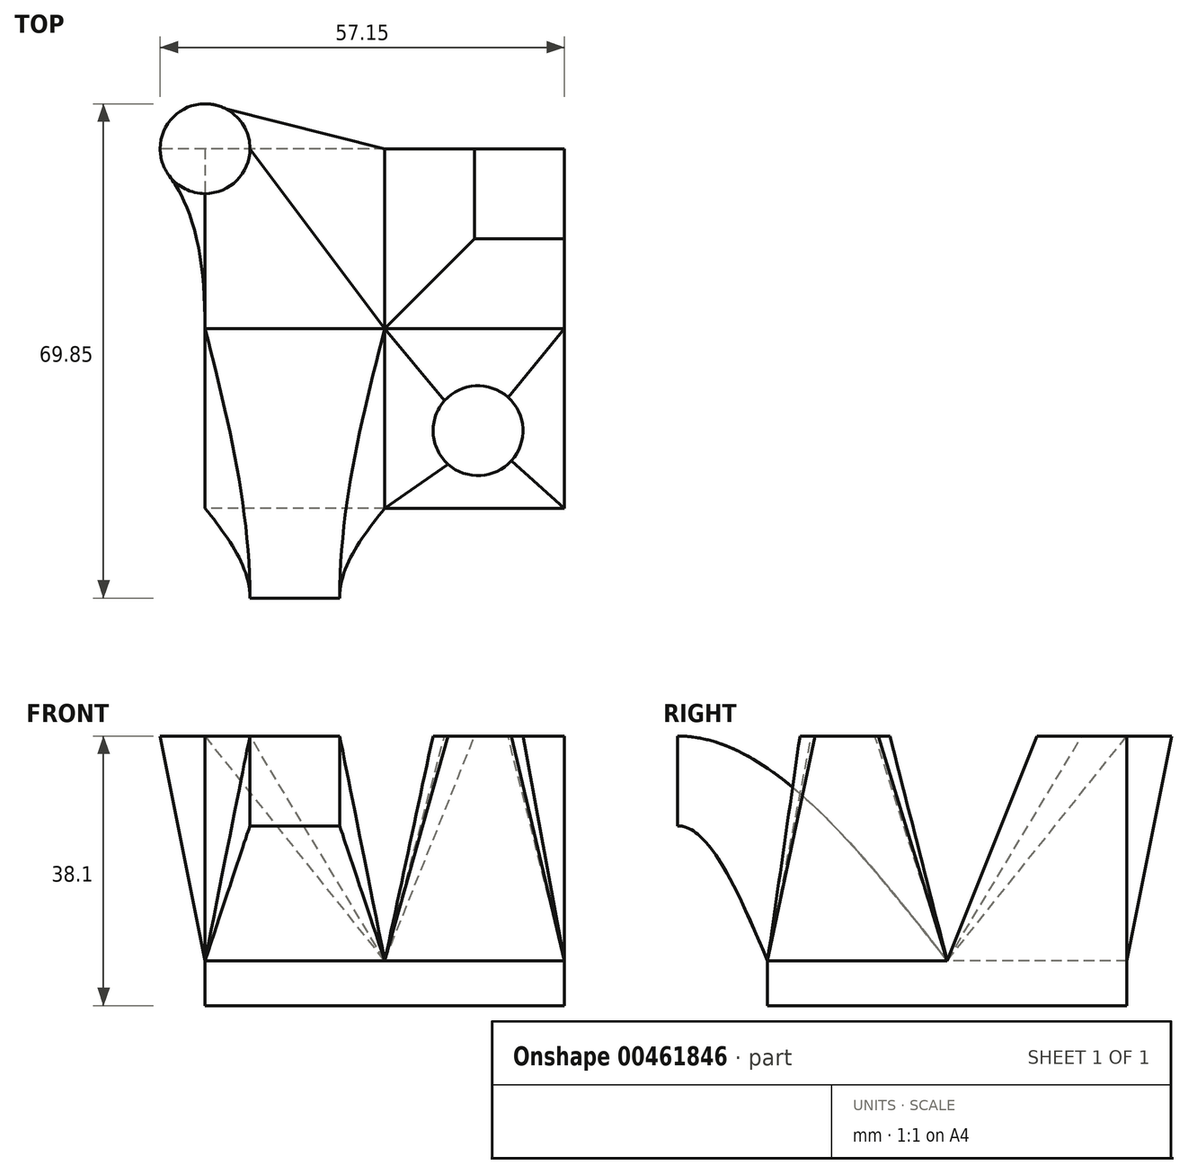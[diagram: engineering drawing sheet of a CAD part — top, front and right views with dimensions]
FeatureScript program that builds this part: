
annotation { "Feature Type Name" : "Feature", "Feature Type Description" : "" }
export const myFeature = defineFeature(function(context is Context, id is Id, definition is map)
    precondition{}
    {
        {
            var Q0;
            Q0=qCreatedBy(makeId("Top.planeOp"),FACE);
            var sketch = newSketch(context, id + "F0", { "sketchPlane" : qUnion([Q0])});
            skLineSegment(sketch, "E0.bottom", {"start": v(25.4, 25.4) * mm, "end": v(-25.4, 25.4) * mm});
            skLineSegment(sketch, "E0.top", {"start": v(25.4, -25.4) * mm, "end": v(-25.4, -25.4) * mm});
            skLineSegment(sketch, "E0.left", {"start": v(25.4, 25.4) * mm, "end": v(25.4, -25.4) * mm});
            skLineSegment(sketch, "E0.right", {"start": v(-25.4, 25.4) * mm, "end": v(-25.4, -25.4) * mm});
            skPoint(sketch, "E0.middle", {"position": v(0, 0) * mm});
            skSolve(sketch);
        }
        {
            var Q0;
            Q0=makeQuery(id+"F0.imprint","IMPRINT",FACE,{"disambiguationData":[TD([[makeQuery(id+"F0.imprint","IMPRINT",EDGE,{"derivedFrom":sQuery(id+"F0.wireOp",EDGE,"E0.bottom")}),1.0]])]});
            extrude(context, id + "F1", {"entities" : qUnion([Q0]), "depth" : 6.35 * mm});
        }
        {
            var Q0;
            Q0=makeQuery(id+"F1.opExtrude","CAP_FACE",FACE,{"disambiguationData":[OSD([sQuery(id+"F0.wireOp",EDGE,"E0.bottom"),sQuery(id+"F0.wireOp",EDGE,"E0.top"),sQuery(id+"F0.wireOp",EDGE,"E0.left"),sQuery(id+"F0.wireOp",EDGE,"E0.right")])],"isStart":false});
            var sketch = newSketch(context, id + "F2", { "sketchPlane" : qUnion([Q0])});
            skLineSegment(sketch, "E1.bottom", {"start": v(0, 0) * mm, "end": v(25.4, 0) * mm});
            skLineSegment(sketch, "E1.top", {"start": v(0, 25.4) * mm, "end": v(25.4, 25.4) * mm});
            skLineSegment(sketch, "E1.left", {"start": v(0, 0) * mm, "end": v(0, 25.4) * mm});
            skLineSegment(sketch, "E1.right", {"start": v(25.4, 0) * mm, "end": v(25.4, 25.4) * mm});
            skSolve(sketch);
        }
        {
            var Q0;
            Q0=qCreatedBy(makeId("Top.planeOp"),FACE);
            cPlane(context, id + "F3", {"entities" : qUnion([Q0]), "cplaneType" : CPlaneType.OFFSET, "offset" : 38.1 * mm, "width" : 152.4 * mm, "height" : 152.4 * mm});
        }
        {
            var Q0;
            Q0=qCreatedBy(id+"F3.planeOp",FACE);
            var sketch = newSketch(context, id + "F4", { "sketchPlane" : qUnion([Q0])});
            skLineSegment(sketch, "E2.bottom", {"start": v(25.4, 25.4) * mm, "end": v(12.7, 25.4) * mm});
            skLineSegment(sketch, "E2.top", {"start": v(25.4, 12.7) * mm, "end": v(12.7, 12.7) * mm});
            skLineSegment(sketch, "E2.left", {"start": v(25.4, 25.4) * mm, "end": v(25.4, 12.7) * mm});
            skLineSegment(sketch, "E2.right", {"start": v(12.7, 25.4) * mm, "end": v(12.7, 12.7) * mm});
            skSolve(sketch);
        }
        {
            var Q1;
            Q1=makeQuery(id+"F2.imprint","IMPRINT",FACE,{"disambiguationData":[TD([[makeQuery(id+"F2.imprint","IMPRINT",EDGE,{"derivedFrom":sQuery(id+"F2.wireOp",EDGE,"E1.bottom")}),1.0]])]});
            var Q2;
            Q2=makeQuery(id+"F4.imprint","IMPRINT",FACE,{"disambiguationData":[TD([[makeQuery(id+"F4.imprint","IMPRINT",EDGE,{"derivedFrom":sQuery(id+"F4.wireOp",EDGE,"E2.bottom")}),1.0]])]});
            loft(context, id + "F5", {"operationType" : NewBodyOperationType.ADD, "sheetProfilesArray" : [{ "sheetProfileEntities" : qUnion([Q1]) }, { "sheetProfileEntities" : qUnion([Q2]) }]});
        }
        {
            var Q0;
            Q0=makeQuery(id+"F1.opExtrude","CAP_FACE",FACE,{"disambiguationData":[OSD([sQuery(id+"F0.wireOp",EDGE,"E0.bottom"),sQuery(id+"F0.wireOp",EDGE,"E0.top"),sQuery(id+"F0.wireOp",EDGE,"E0.left"),sQuery(id+"F0.wireOp",EDGE,"E0.right")])],"isStart":false});
            var sketch = newSketch(context, id + "F6", { "sketchPlane" : qUnion([Q0])});
            skLineSegment(sketch, "E3.bottom", {"start": v(0, 0) * mm, "end": v(25.4, 0) * mm});
            skLineSegment(sketch, "E3.top", {"start": v(0, -25.4) * mm, "end": v(25.4, -25.4) * mm});
            skLineSegment(sketch, "E3.left", {"start": v(0, 0) * mm, "end": v(0, -25.4) * mm});
            skLineSegment(sketch, "E3.right", {"start": v(25.4, 0) * mm, "end": v(25.4, -25.4) * mm});
            skSolve(sketch);
        }
        {
            var Q0;
            Q0=qCreatedBy(id+"F3.planeOp",FACE);
            var sketch = newSketch(context, id + "F7", { "sketchPlane" : qUnion([Q0])});
            skCircle(sketch, "E4", {"center": v(13.18, -14.46) * mm, "radius": 6.35 * mm});
            skLineSegment(sketch, "E5", {"start": v(-12.76, -14.46) * mm, "end": v(47.83, -14.46) * mm, "construction": true});
            skLineSegment(sketch, "E6", {"start": v(13.18, -44.22) * mm, "end": v(13.18, 0) * mm, "construction": true});
            skSolve(sketch);
        }
        {
            var Q1;
            Q1=makeQuery(id+"F6.imprint","IMPRINT",FACE,{"disambiguationData":[TD([[makeQuery(id+"F6.imprint","IMPRINT",EDGE,{"derivedFrom":sQuery(id+"F6.wireOp",EDGE,"E3.bottom")}),-1.0]])]});
            var Q2;
            Q2=makeQuery(id+"F7.imprint","IMPRINT",FACE,{"disambiguationData":[TD([[makeQuery(id+"F7.imprint","IMPRINT",EDGE,{"derivedFrom":sQuery(id+"F7.wireOp",EDGE,"E4")}),1.0]])]});
            loft(context, id + "F8", {"operationType" : NewBodyOperationType.ADD, "sheetProfilesArray" : [{ "sheetProfileEntities" : qUnion([Q1]) }, { "sheetProfileEntities" : qUnion([Q2]) }]});
        }
        {
            var Q0;
            Q0=makeQuery(id+"F1.opExtrude","CAP_FACE",FACE,{"disambiguationData":[OSD([sQuery(id+"F0.wireOp",EDGE,"E0.bottom"),sQuery(id+"F0.wireOp",EDGE,"E0.top"),sQuery(id+"F0.wireOp",EDGE,"E0.left"),sQuery(id+"F0.wireOp",EDGE,"E0.right")])],"isStart":false});
            var sketch = newSketch(context, id + "F9", { "sketchPlane" : qUnion([Q0])});
            skLineSegment(sketch, "E7.bottom", {"start": v(0, 0) * mm, "end": v(-25.4, 0) * mm});
            skLineSegment(sketch, "E7.top", {"start": v(0, 25.4) * mm, "end": v(-25.4, 25.4) * mm});
            skLineSegment(sketch, "E7.left", {"start": v(0, 0) * mm, "end": v(0, 25.4) * mm});
            skLineSegment(sketch, "E7.right", {"start": v(-25.4, 0) * mm, "end": v(-25.4, 25.4) * mm});
            skSolve(sketch);
        }
        {
            var Q0;
            Q0=qCreatedBy(id+"F3.planeOp",FACE);
            var sketch = newSketch(context, id + "F10", { "sketchPlane" : qUnion([Q0])});
            skCircle(sketch, "E8", {"center": v(-25.4, 25.4) * mm, "radius": 6.35 * mm});
            skSolve(sketch);
        }
        {
            var Q1;
            Q1=makeQuery(id+"F9.imprint","IMPRINT",FACE,{"disambiguationData":[TD([[makeQuery(id+"F9.imprint","IMPRINT",EDGE,{"derivedFrom":sQuery(id+"F9.wireOp",EDGE,"E7.bottom")}),-1.0]])]});
            var Q2;
            Q2=makeQuery(id+"F10.imprint","IMPRINT",FACE,{"disambiguationData":[TD([[makeQuery(id+"F10.imprint","IMPRINT",EDGE,{"derivedFrom":sQuery(id+"F10.wireOp",EDGE,"E8")}),1.0]])]});
            loft(context, id + "F11", {"operationType" : NewBodyOperationType.ADD, "sheetProfilesArray" : [{ "sheetProfileEntities" : qUnion([Q1]) }, { "sheetProfileEntities" : qUnion([Q2]) }]});
        }
        {
            var Q0;
            Q0=qCreatedBy(makeId("Front.planeOp"),FACE);
            cPlane(context, id + "F12", {"entities" : qUnion([Q0]), "cplaneType" : CPlaneType.OFFSET, "offset" : 38.1 * mm, "width" : 152.4 * mm, "height" : 152.4 * mm});
        }
        {
            var Q0;
            Q0=qCreatedBy(id+"F12.planeOp",FACE);
            var sketch = newSketch(context, id + "F13", { "sketchPlane" : qUnion([Q0])});
            skLineSegment(sketch, "E9.bottom", {"start": v(-6.37, 38.1) * mm, "end": v(-19.07, 38.1) * mm});
            skLineSegment(sketch, "E9.top", {"start": v(-6.37, 25.4) * mm, "end": v(-19.07, 25.4) * mm});
            skLineSegment(sketch, "E9.left", {"start": v(-6.37, 38.1) * mm, "end": v(-6.37, 25.4) * mm});
            skLineSegment(sketch, "E9.right", {"start": v(-19.07, 38.1) * mm, "end": v(-19.07, 25.4) * mm});
            skSolve(sketch);
        }
        {
            var Q1;
            Q1=makeQuery(id+"F13.imprint","IMPRINT",FACE,{"disambiguationData":[TD([[makeQuery(id+"F13.imprint","IMPRINT",EDGE,{"derivedFrom":sQuery(id+"F13.wireOp",EDGE,"E9.bottom")}),1.0]])]});
            var Q2;
            Q2=makeQuery(id+"F1.opExtrude","CAP_FACE",FACE,{"disambiguationData":[OSD([sQuery(id+"F0.wireOp",EDGE,"E0.bottom"),sQuery(id+"F0.wireOp",EDGE,"E0.top"),sQuery(id+"F0.wireOp",EDGE,"E0.left"),sQuery(id+"F0.wireOp",EDGE,"E0.right")])],"isStart":false});
            var Q3;
            Q3=sQuery(id+"F13.wireOp",VERTEX,"E9.right.start");
            var Q4;
            Q4=makeQuery(id+"F11.opLoft","MID_CAP_VERTEX",VERTEX,{"disambiguationData":[OSD([sQuery(id+"F0.wireOp",EDGE,"E0.right"),sQuery(id+"F9.wireOp",EDGE,"E7.bottom"),sQuery(id+"F9.wireOp",EDGE,"E7.right")])],"capPos":0.0});
            loft(context, id + "F14", {"operationType" : NewBodyOperationType.ADD, "startCondition" : LoftEndDerivativeType.NORMAL_TO_PROFILE, "startMagnitude" : 1, "sheetProfilesArray" : [{ "sheetProfileEntities" : qUnion([Q1]) }, { "sheetProfileEntities" : qUnion([Q2]) }], "matchConnections" : true, "connections" : [{ "connectionEntities" : qUnion([Q3, Q4]), "connectionEdgeQueries" : qUnion([]), "connectionEdgeParameters" : [] }]});
        }
    });
